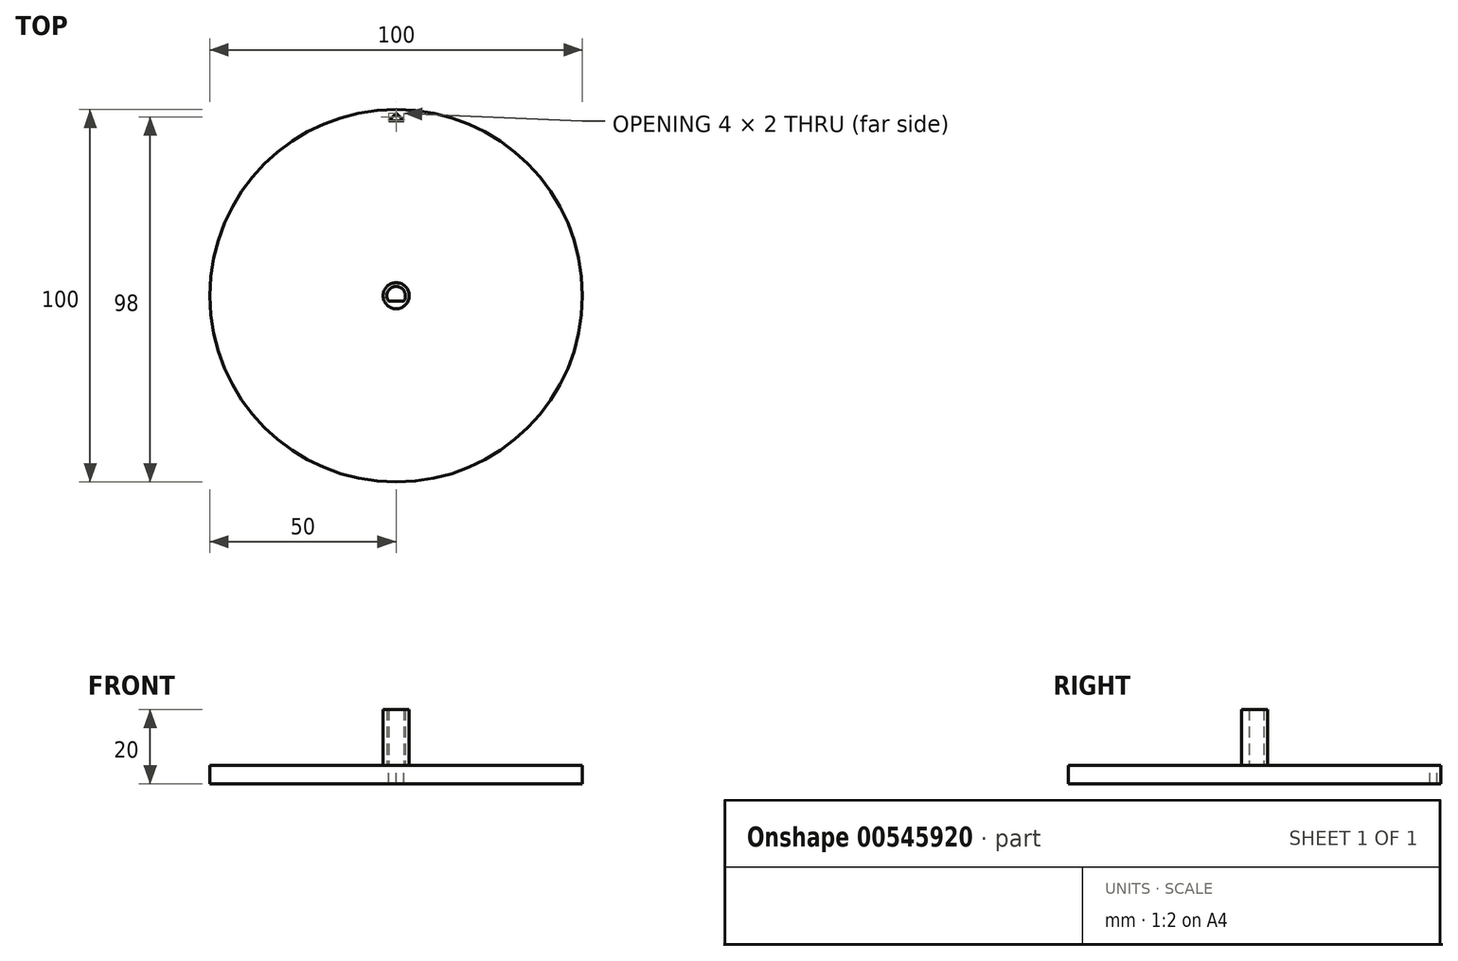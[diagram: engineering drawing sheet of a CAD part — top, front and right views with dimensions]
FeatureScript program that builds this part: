
annotation { "Feature Type Name" : "Feature", "Feature Type Description" : "" }
export const myFeature = defineFeature(function(context is Context, id is Id, definition is map)
    precondition{}
    {
        {
            var Q0;
            Q0=qCreatedBy(makeId("Top.planeOp"),FACE);
            var sketch = newSketch(context, id + "F0", { "sketchPlane" : qUnion([Q0])});
            skCircle(sketch, "E0", {"center": v(0, 0) * mm, "radius": 2.5 * mm});
            skLineSegment(sketch, "E1", {"start": v(0, 0) * mm, "end": v(0, -1.5) * mm});
            skLineSegment(sketch, "E2", {"start": v(0, -1.5) * mm, "end": v(2, -1.5) * mm});
            skLineSegment(sketch, "E3", {"start": v(0, -1.5) * mm, "end": v(-2, -1.5) * mm});
            skCircle(sketch, "E4", {"center": v(0, 0) * mm, "radius": 3.5 * mm});
            skCircle(sketch, "E5", {"center": v(0, 0) * mm, "radius": 150 * mm});
            skSolve(sketch);
        }
        {
            var Q0;
            {var subQ0=sQuery(id+"F0.wireOp",EDGE,"E2");Q0=makeQuery(id+"F0.imprint","IMPRINT",FACE,{"disambiguationData":[TD([[makeQuery(id+"F0.imprint","IMPRINT",EDGE,{"derivedFrom":subQ0}),-1.0]])]});}
            var Q1;
            Q1=makeQuery(id+"F0.imprint","IMPRINT",FACE,{"disambiguationData":[TD([[makeQuery(id+"F0.imprint","IMPRINT",EDGE,{"derivedFrom":sQuery(id+"F0.wireOp",EDGE,"E4")}),1.0]])]});
            extrude(context, id + "F1", {"entities" : qUnion([Q0, Q1]), "depth" : 15 * mm, "offsetDistance" : 25 * mm});
        }
        {
            var Q0;
            Q0=qCreatedBy(makeId("Top.planeOp"),FACE);
            var sketch = newSketch(context, id + "F2", { "sketchPlane" : qUnion([Q0])});
            skCircle(sketch, "E6", {"center": v(0, 0) * mm, "radius": 50 * mm});
            skLineSegment(sketch, "E7", {"start": v(0, 0) * mm, "end": v(0, 50) * mm});
            skLineSegment(sketch, "E8", {"start": v(0, 50) * mm, "end": v(0, 47) * mm});
            skLineSegment(sketch, "E9", {"start": v(0, 47) * mm, "end": v(2, 47) * mm});
            skLineSegment(sketch, "E10", {"start": v(2, 47) * mm, "end": v(-2, 47) * mm});
            skLineSegment(sketch, "E11", {"start": v(-2, 47) * mm, "end": v(0, 47) * mm});
            skLineSegment(sketch, "E12", {"start": v(0, 47) * mm, "end": v(0, 49) * mm});
            skLineSegment(sketch, "E13", {"start": v(0, 49) * mm, "end": v(-2, 47) * mm});
            skLineSegment(sketch, "E14", {"start": v(0, 49) * mm, "end": v(2, 47) * mm});
            skSolve(sketch);
        }
        {
            var Q0;
            Q0 = qSketchRegion(id + "F2", true);
            extrude(context, id + "F3", {"entities" : qUnion([Q0]), "operationType" : NewBodyOperationType.ADD, "oppositeDirection" : true, "depth" : 5 * mm, "offsetDistance" : 25 * mm});
        }
    });
